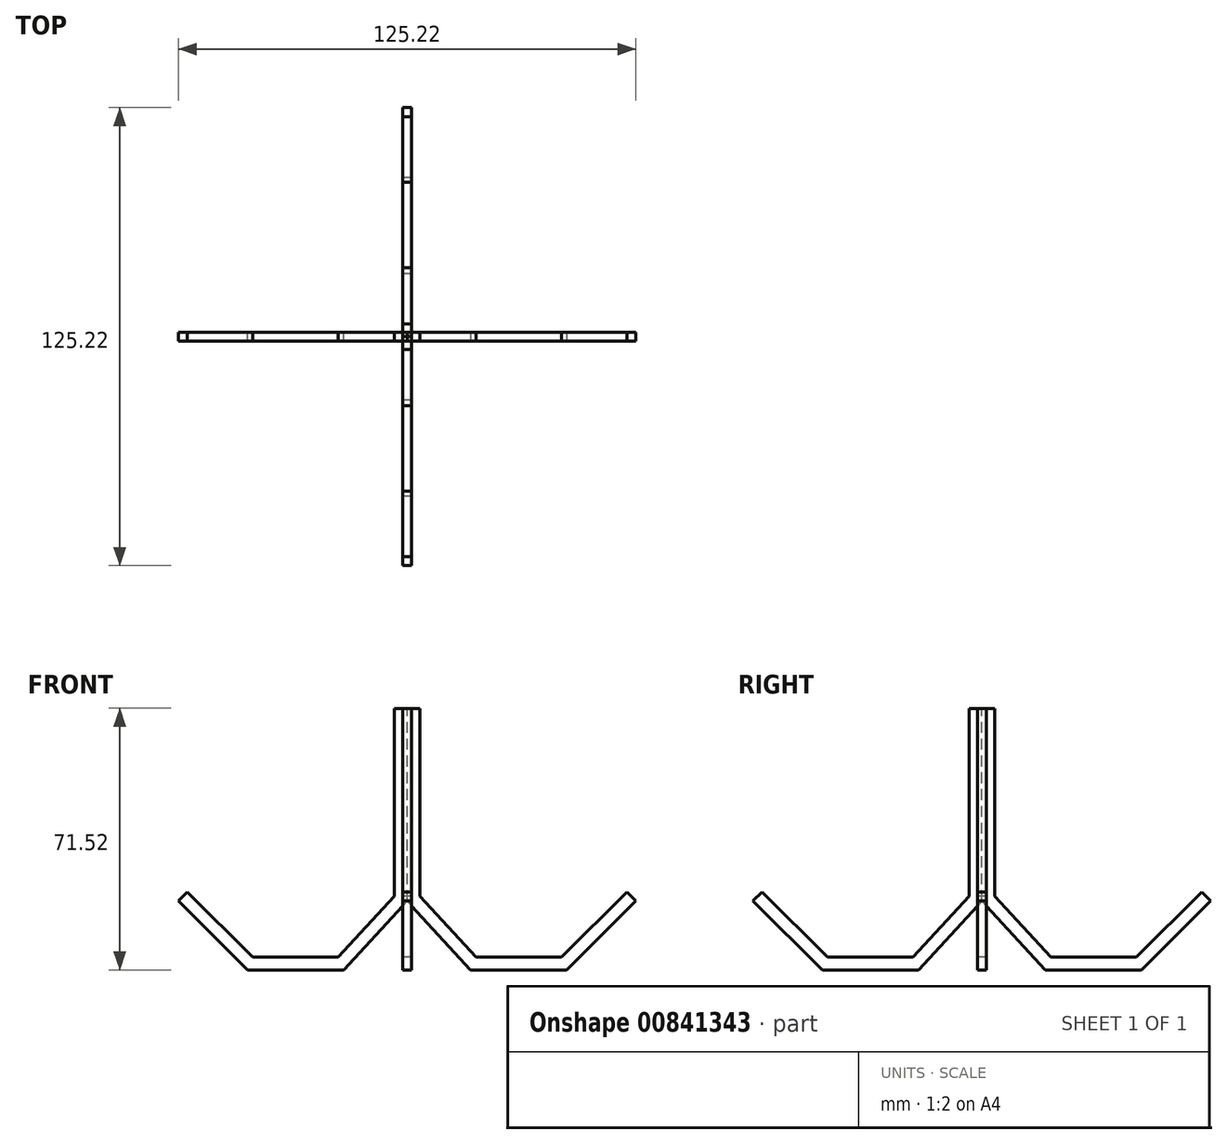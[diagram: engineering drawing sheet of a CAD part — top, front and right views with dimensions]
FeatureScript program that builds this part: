
annotation { "Feature Type Name" : "Feature", "Feature Type Description" : "" }
export const myFeature = defineFeature(function(context is Context, id is Id, definition is map)
    precondition{}
    {
        {
            var Q0;
            Q0=qCreatedBy(makeId("Front.planeOp"),FACE);
            var sketch = newSketch(context, id + "F0", { "sketchPlane" : qUnion([Q0])});
            skLineSegment(sketch, "E0", {"start": v(0, 0) * mm, "end": v(0, 52.69) * mm});
            skLineSegment(sketch, "E1", {"start": v(0, 0) * mm, "end": v(-17.37, -18.83) * mm});
            skLineSegment(sketch, "E2", {"start": v(-17.37, -18.83) * mm, "end": v(-43.64, -18.83) * mm});
            skLineSegment(sketch, "E3", {"start": v(-43.64, -18.83) * mm, "end": v(-62.6, 0) * mm});
            skLineSegment(sketch, "E4.0", {"start": v(-42.2, -15.33) * mm, "end": v(-60.14, 2.48) * mm});
            skLineSegment(sketch, "E4.1", {"start": v(-18.9, -15.33) * mm, "end": v(-42.2, -15.33) * mm});
            skLineSegment(sketch, "E4.2", {"start": v(-3.5, 1.37) * mm, "end": v(-18.9, -15.33) * mm});
            skLineSegment(sketch, "E4.3", {"start": v(-3.5, 1.37) * mm, "end": v(-3.5, 52.69) * mm});
            skLineSegment(sketch, "E5", {"start": v(-60.14, 2.48) * mm, "end": v(-62.6, 0) * mm});
            skLineSegment(sketch, "E6", {"start": v(-3.5, 52.69) * mm, "end": v(0, 52.69) * mm});
            skSolve(sketch);
        }
        {
            var Q0;
            Q0=makeQuery(id+"F0.imprint","IMPRINT",FACE,{"disambiguationData":[TD([[makeQuery(id+"F0.imprint","IMPRINT",EDGE,{"derivedFrom":sQuery(id+"F0.wireOp",EDGE,"E0")}),1.0]])]});
            extrude(context, id + "F1", {"entities" : qUnion([Q0]), "endBound" : BoundingType.SYMMETRIC, "depth" : 2.5 * mm, "offsetDistance" : 25 * mm});
        }
        {
            var Q0;
            Q0=makeQuery(id+"F1.opExtrude","SWEPT_BODY",BODY,{"disambiguationData":[OSD([sQuery(id+"F0.wireOp",EDGE,"E0"),sQuery(id+"F0.wireOp",EDGE,"E1"),sQuery(id+"F0.wireOp",EDGE,"E2"),sQuery(id+"F0.wireOp",EDGE,"E3"),sQuery(id+"F0.wireOp",EDGE,"E4.0"),sQuery(id+"F0.wireOp",EDGE,"E4.1"),sQuery(id+"F0.wireOp",EDGE,"E4.2"),sQuery(id+"F0.wireOp",EDGE,"E4.3"),sQuery(id+"F0.wireOp",EDGE,"E5"),sQuery(id+"F0.wireOp",EDGE,"E6")])]});
            var Q1;
            Q1=sQuery(id+"F0.wireOp",EDGE,"E0");
            circularPattern(context, id + "F2", {"entities" : qUnion([Q0]), "axis" : qUnion([Q1]), "angle" : 360 * degree, "instanceCount" : 4, "equalSpace" : true});
        }
    });
